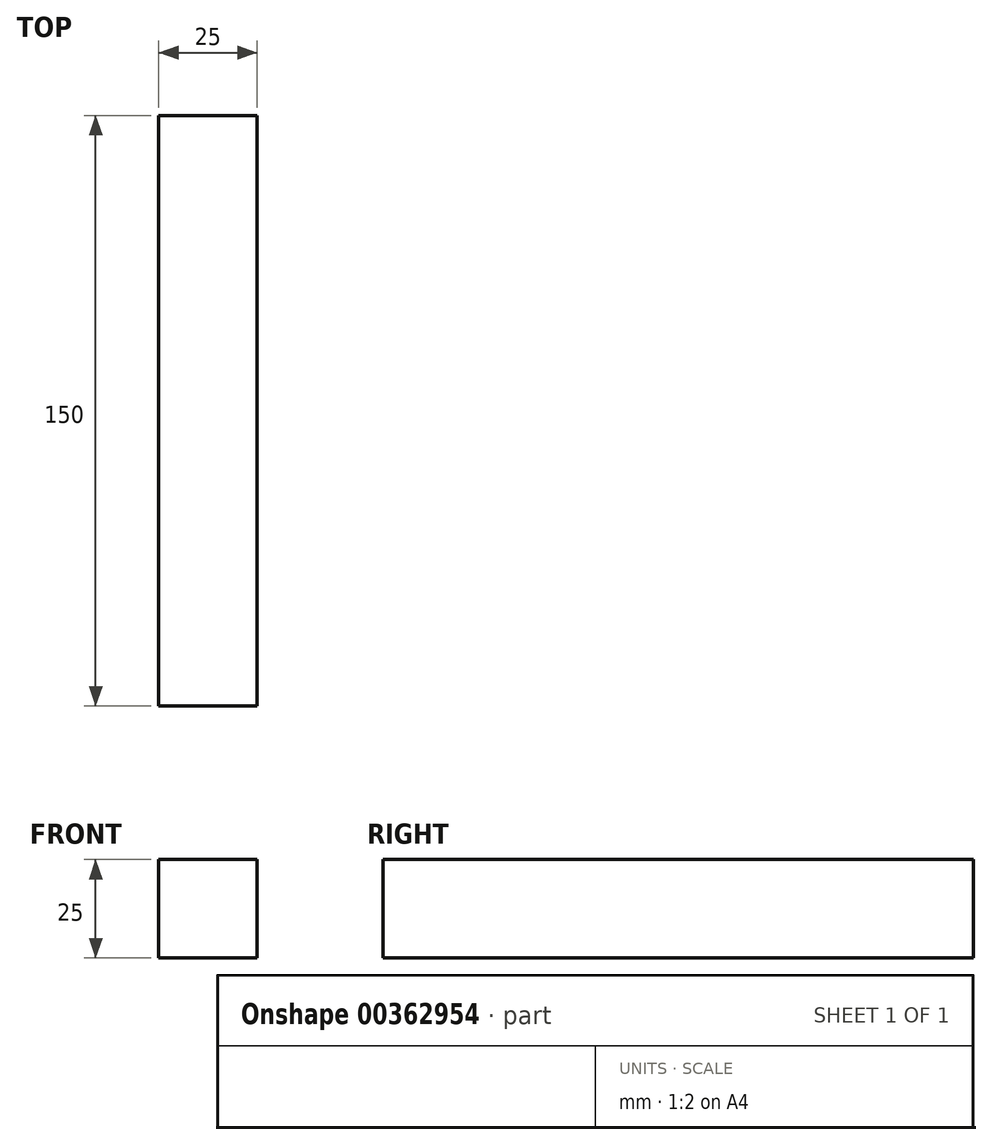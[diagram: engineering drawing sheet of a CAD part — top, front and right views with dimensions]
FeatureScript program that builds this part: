
annotation { "Feature Type Name" : "Feature", "Feature Type Description" : "" }
export const myFeature = defineFeature(function(context is Context, id is Id, definition is map)
    precondition{}
    {
        {
            var Q0;
            Q0=qCreatedBy(makeId("Front.planeOp"),FACE);
            var sketch = newSketch(context, id + "F0", { "sketchPlane" : qUnion([Q0])});
            skLineSegment(sketch, "E0.bottom", {"start": v(-7.08, -17.52) * mm, "end": v(-32.08, -17.52) * mm});
            skLineSegment(sketch, "E0.top", {"start": v(-7.08, 7.48) * mm, "end": v(-32.08, 7.48) * mm});
            skLineSegment(sketch, "E0.left", {"start": v(-7.08, -17.52) * mm, "end": v(-7.08, 7.48) * mm});
            skLineSegment(sketch, "E0.right", {"start": v(-32.08, -17.52) * mm, "end": v(-32.08, 7.48) * mm});
            skSolve(sketch);
        }
        {
            var Q0;
            Q0=makeQuery(id+"F0.imprint","IMPRINT",FACE,{"disambiguationData":[TD([[makeQuery(id+"F0.imprint","IMPRINT",EDGE,{"derivedFrom":sQuery(id+"F0.wireOp",EDGE,"E0.bottom")}),-1.0]])]});
            extrude(context, id + "F1", {"entities" : qUnion([Q0]), "depth" : 150 * mm});
        }
    });
